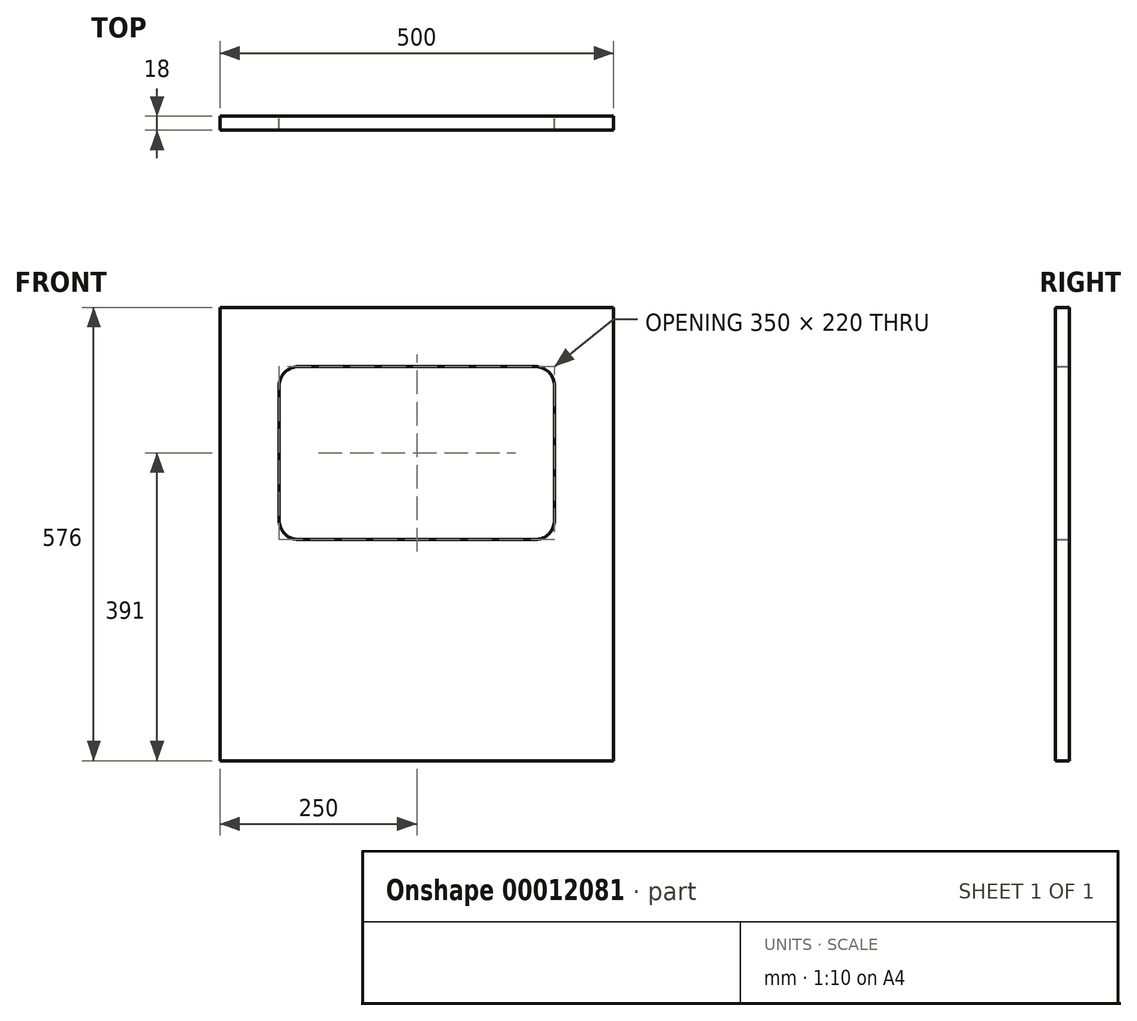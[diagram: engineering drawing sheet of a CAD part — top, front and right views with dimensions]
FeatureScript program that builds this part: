
annotation { "Feature Type Name" : "Feature", "Feature Type Description" : "" }
export const myFeature = defineFeature(function(context is Context, id is Id, definition is map)
    precondition{}
    {
        {
            var Q0;
            Q0=qCreatedBy(makeId("Front.planeOp"),FACE);
            var sketch = newSketch(context, id + "F0", { "sketchPlane" : qUnion([Q0])});
            skLineSegment(sketch, "E0.rect.bottom", {"start": v(-250, 288) * mm, "end": v(250, 288) * mm});
            skLineSegment(sketch, "E0.rect.top", {"start": v(-250, -288) * mm, "end": v(250, -288) * mm});
            skLineSegment(sketch, "E0.rect.left", {"start": v(-250, 288) * mm, "end": v(-250, -288) * mm});
            skLineSegment(sketch, "E0.rect.right", {"start": v(250, 288) * mm, "end": v(250, -288) * mm});
            skPoint(sketch, "E0.rect.middle", {"position": v(0, 0) * mm});
            skLineSegment(sketch, "E1.bottom", {"start": v(-150, 213) * mm, "end": v(150, 213) * mm});
            skLineSegment(sketch, "E1.top", {"start": v(-150, -7) * mm, "end": v(150, -7) * mm});
            skLineSegment(sketch, "E1.left", {"start": v(-175, 188) * mm, "end": v(-175, 18) * mm});
            skLineSegment(sketch, "E1.right", {"start": v(175, 188) * mm, "end": v(175, 18) * mm});
            skPoint(sketch, "E2.visualSharp", {"position": v(-175, 213) * mm});
            skArc(sketch, "E2.filletArc", {"start": v(-150, 213) * mm, "mid": v(-167.68, 205.68) * mm, "end": v(-175, 188) * mm});
            skPoint(sketch, "E3.visualSharp", {"position": v(-175, -7) * mm});
            skArc(sketch, "E3.filletArc", {"start": v(-175, 18) * mm, "mid": v(-167.68, 0.32) * mm, "end": v(-150, -7) * mm});
            skPoint(sketch, "E4.visualSharp", {"position": v(175, -7) * mm});
            skArc(sketch, "E4.filletArc", {"start": v(150, -7) * mm, "mid": v(167.68, 0.32) * mm, "end": v(175, 18) * mm});
            skPoint(sketch, "E5.visualSharp", {"position": v(175, 213) * mm});
            skArc(sketch, "E5.filletArc", {"start": v(175, 188) * mm, "mid": v(167.68, 205.68) * mm, "end": v(150, 213) * mm});
            skSolve(sketch);
        }
        {
            var Q0;
            Q0 = qSketchRegion(id + "F0", true);
            extrude(context, id + "F1", {"entities" : qUnion([Q0]), "depth" : 18 * mm});
        }
    });
